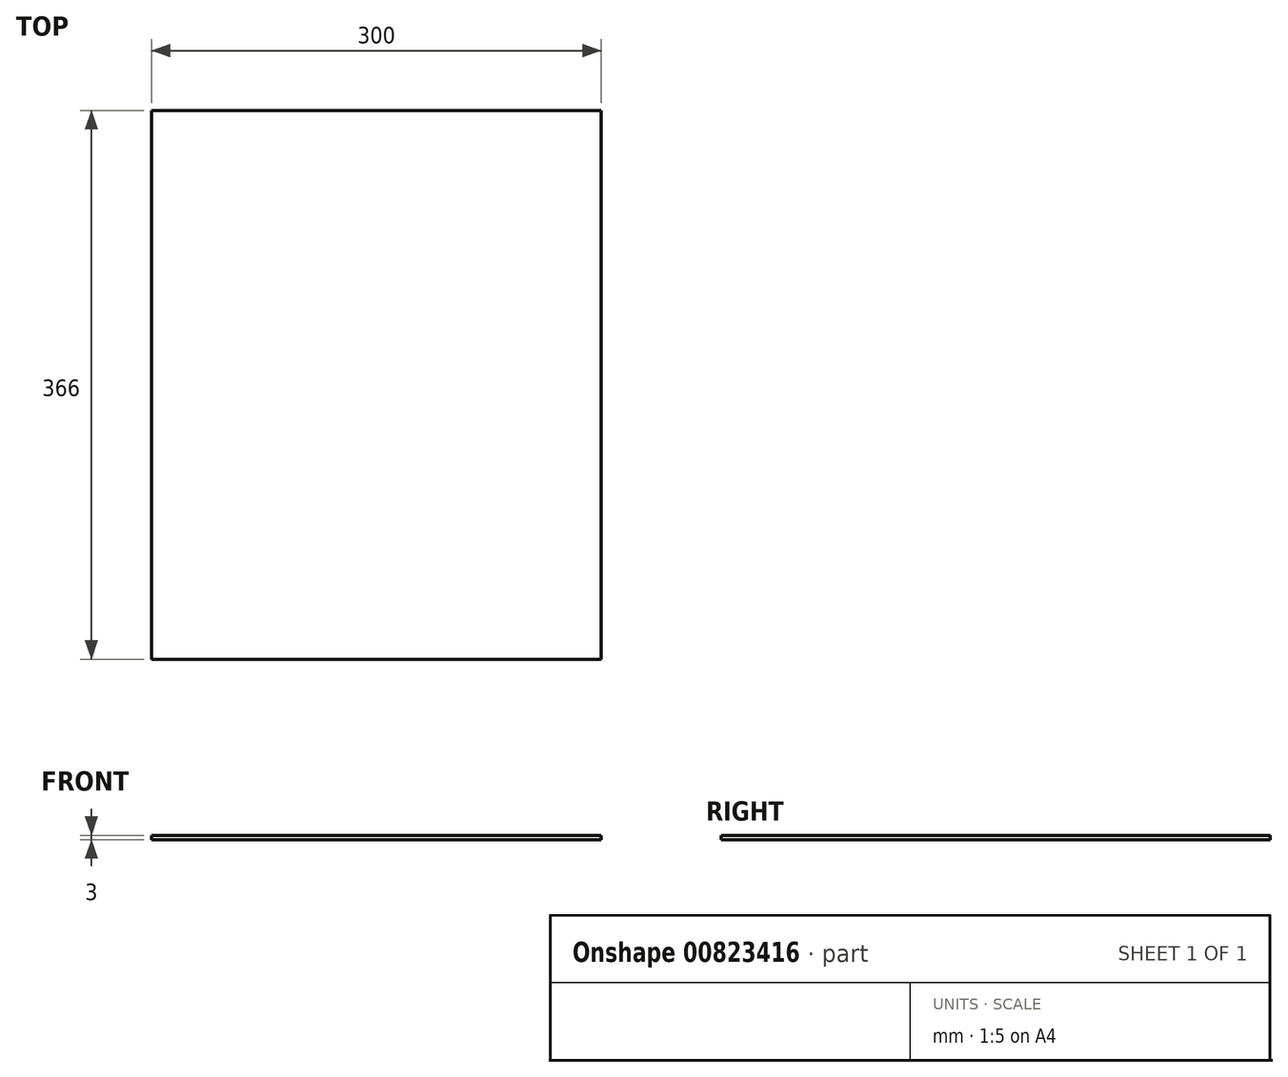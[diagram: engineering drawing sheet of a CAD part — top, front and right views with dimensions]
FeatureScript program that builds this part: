
annotation { "Feature Type Name" : "Feature", "Feature Type Description" : "" }
export const myFeature = defineFeature(function(context is Context, id is Id, definition is map)
    precondition{}
    {
        {
            var Q0;
            Q0=qCreatedBy(makeId("Top.planeOp"),FACE);
            var sketch = newSketch(context, id + "F0", { "sketchPlane" : qUnion([Q0])});
            skLineSegment(sketch, "E0.bottom", {"start": v(-150, 183) * mm, "end": v(150, 183) * mm});
            skLineSegment(sketch, "E0.top", {"start": v(-150, -183) * mm, "end": v(150, -183) * mm});
            skLineSegment(sketch, "E0.left", {"start": v(-150, 183) * mm, "end": v(-150, -183) * mm});
            skLineSegment(sketch, "E0.right", {"start": v(150, 183) * mm, "end": v(150, -183) * mm});
            skPoint(sketch, "E0.middle", {"position": v(0, 0) * mm});
            skSolve(sketch);
        }
        {
            var Q0;
            Q0=makeQuery(id+"F0.imprint","IMPRINT",FACE,{"disambiguationData":[TD([[makeQuery(id+"F0.imprint","IMPRINT",EDGE,{"derivedFrom":sQuery(id+"F0.wireOp",EDGE,"E0.bottom")}),-1.0]])]});
            extrude(context, id + "F1", {"entities" : qUnion([Q0]), "depth" : 3 * mm, "offsetDistance" : 25 * mm});
        }
    });
